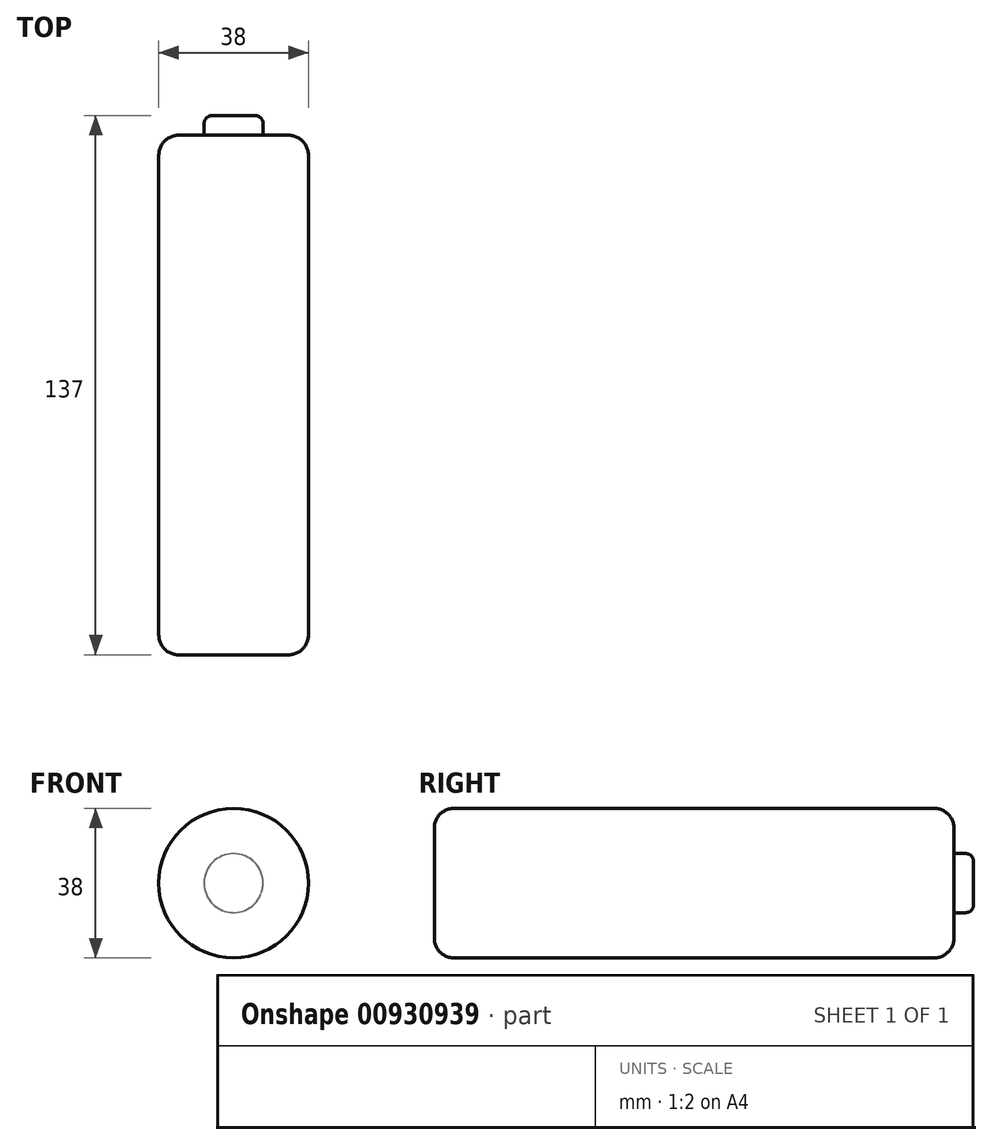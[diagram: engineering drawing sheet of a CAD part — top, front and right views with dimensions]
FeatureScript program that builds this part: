
annotation { "Feature Type Name" : "Feature", "Feature Type Description" : "" }
export const myFeature = defineFeature(function(context is Context, id is Id, definition is map)
    precondition{}
    {
        {
            var Q0;
            Q0=qCreatedBy(makeId("Front.planeOp"),FACE);
            var sketch = newSketch(context, id + "F0", { "sketchPlane" : qUnion([Q0])});
            skCircle(sketch, "E0", {"center": v(0, 0) * mm, "radius": 19 * mm});
            skSolve(sketch);
        }
        {
            var Q0;
            Q0 = qSketchRegion(id + "F0", true);
            extrude(context, id + "F1", {"entities" : qUnion([Q0]), "depth" : 132 * mm, "offsetDistance" : 25 * mm});
        }
        {
            var Q0;
            Q0=makeQuery(id+"F1.opExtrude","CAP_EDGE",EDGE,{"disambiguationData":[OSD([sQuery(id+"F0.wireOp",EDGE,"E0")])],"isStart":false});
            var Q1;
            Q1=makeQuery(id+"F1.opExtrude","CAP_EDGE",EDGE,{"disambiguationData":[OSD([sQuery(id+"F0.wireOp",EDGE,"E0")])],"isStart":true});
            fillet(context, id + "F2", {"entities" : qUnion([Q0, Q1]), "radius" : 5 * mm, "tangentPropagation" : true, "allowEdgeOverflow" : false});
        }
        {
            var Q0;
            Q0=makeQuery(id+"F1.opExtrude","CAP_FACE",FACE,{"disambiguationData":[OSD([sQuery(id+"F0.wireOp",EDGE,"E0")])],"isStart":true});
            var sketch = newSketch(context, id + "F3", { "sketchPlane" : qUnion([Q0])});
            skCircle(sketch, "E1", {"center": v(0, 0) * mm, "radius": 7.5 * mm});
            skSolve(sketch);
        }
        {
            var Q0;
            Q0=makeQuery(id+"F3.imprint","IMPRINT",FACE,{"disambiguationData":[TD([[makeQuery(id+"F3.imprint","IMPRINT",EDGE,{"derivedFrom":sQuery(id+"F3.wireOp",EDGE,"E1")}),1.0]])]});
            extrude(context, id + "F4", {"entities" : qUnion([Q0]), "operationType" : NewBodyOperationType.ADD, "depth" : 5 * mm, "offsetDistance" : 25 * mm});
        }
        {
            var Q0;
            Q0=makeQuery(id+"F4.opExtrude","CAP_EDGE",EDGE,{"disambiguationData":[OSD([sQuery(id+"F3.wireOp",EDGE,"E1")])],"isStart":false});
            fillet(context, id + "F5", {"entities" : qUnion([Q0]), "radius" : 2 * mm, "tangentPropagation" : true, "allowEdgeOverflow" : false});
        }
    });
